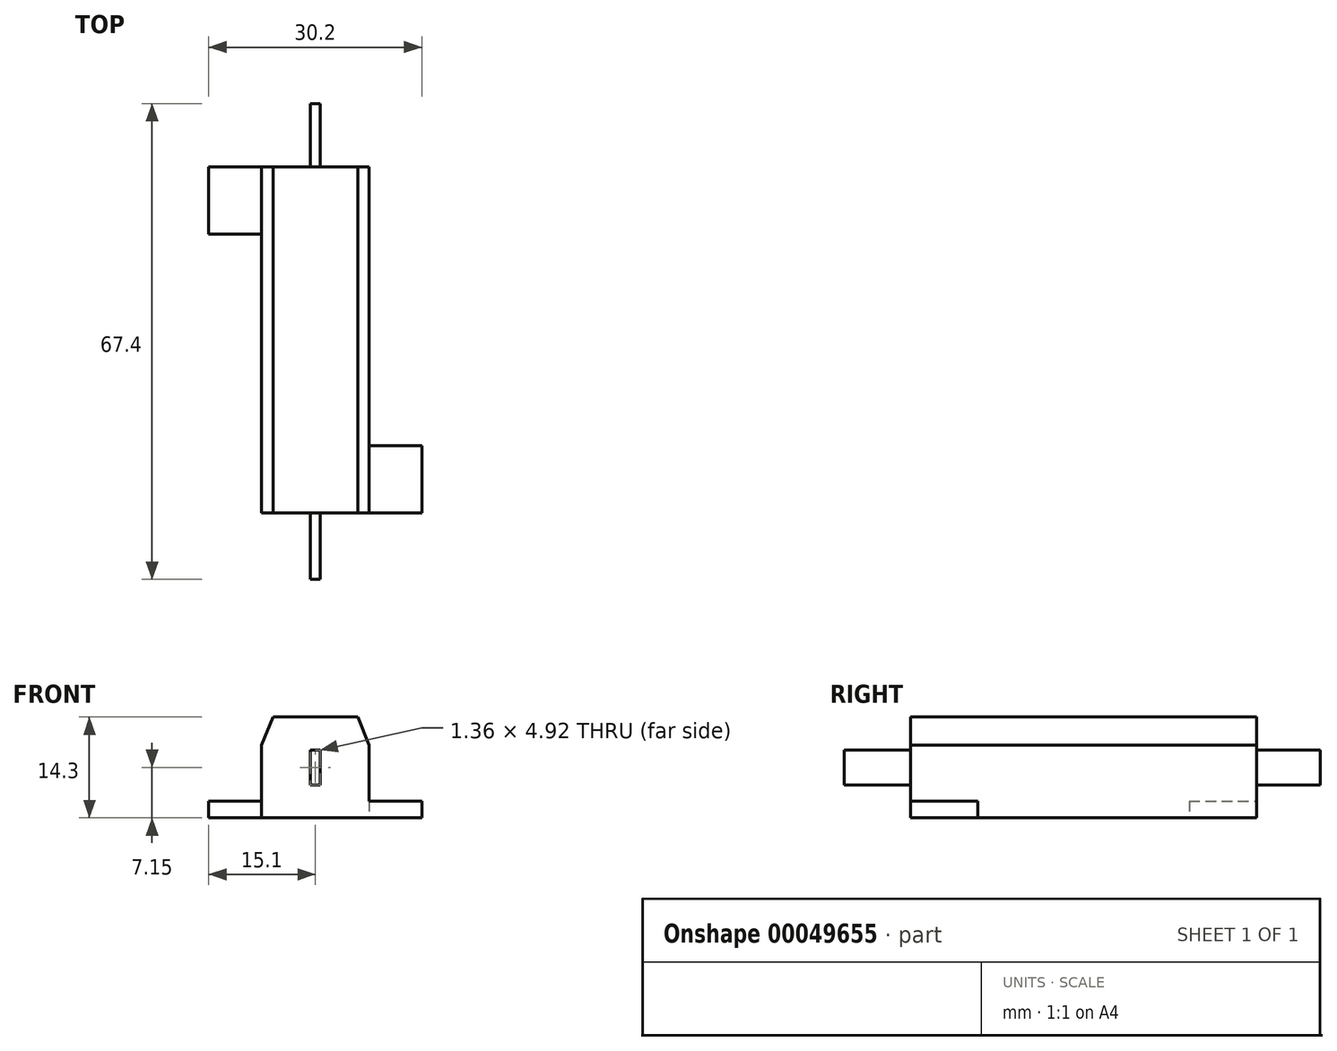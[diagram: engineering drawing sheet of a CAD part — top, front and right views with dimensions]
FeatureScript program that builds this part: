
annotation { "Feature Type Name" : "Feature", "Feature Type Description" : "" }
export const myFeature = defineFeature(function(context is Context, id is Id, definition is map)
    precondition{}
    {
        {
            var Q0;
            Q0=qCreatedBy(makeId("Front.planeOp"),FACE);
            var sketch = newSketch(context, id + "F0", { "sketchPlane" : qUnion([Q0])});
            skLineSegment(sketch, "E0.bottom", {"start": v(0, 0) * mm, "end": v(-15.2, 0) * mm});
            skLineSegment(sketch, "E0.top", {"start": v(0, 2.41) * mm, "end": v(-15.2, 2.4) * mm, "construction": true});
            skLineSegment(sketch, "E0.left", {"start": v(0, 0) * mm, "end": v(0, 2.4) * mm});
            skLineSegment(sketch, "E0.right", {"start": v(-15.2, 0) * mm, "end": v(-15.2, 2.4) * mm});
            skLineSegment(sketch, "E1", {"start": v(-1.6, 14.3) * mm, "end": v(-13.6, 14.3) * mm});
            skLineSegment(sketch, "E2", {"start": v(0, 2.41) * mm, "end": v(0, 10.3) * mm});
            skLineSegment(sketch, "E3", {"start": v(-7.6, 0) * mm, "end": v(-7.6, 14.3) * mm, "construction": true});
            skLineSegment(sketch, "E4", {"start": v(0, 10.3) * mm, "end": v(-1.6, 14.3) * mm});
            skLineSegment(sketch, "E5", {"start": v(-15.2, 2.4) * mm, "end": v(-15.2, 10.3) * mm});
            skLineSegment(sketch, "E6", {"start": v(-15.2, 10.3) * mm, "end": v(-13.6, 14.3) * mm});
            skSolve(sketch);
        }
        {
            var Q0;
            Q0=makeQuery(id+"F0.imprint","IMPRINT",FACE,{"disambiguationData":[TD([[makeQuery(id+"F0.imprint","IMPRINT",EDGE,{"derivedFrom":sQuery(id+"F0.wireOp",EDGE,"E0.bottom")}),-1.0]])]});
            extrude(context, id + "F1", {"entities" : qUnion([Q0]), "depth" : 49 * mm});
        }
        {
            var Q0;
            Q0=makeQuery(id+"F1.opExtrude","SWEPT_FACE",FACE,{"disambiguationData":[OSD([sQuery(id+"F0.wireOp",EDGE,"E0.bottom")])]});
            var sketch = newSketch(context, id + "F2", { "sketchPlane" : qUnion([Q0])});
            skLineSegment(sketch, "E7.bottom", {"start": v(-15.2, 0) * mm, "end": v(-22.7, 0) * mm});
            skLineSegment(sketch, "E7.top", {"start": v(-15.2, 9.53) * mm, "end": v(-22.7, 9.53) * mm});
            skLineSegment(sketch, "E7.left", {"start": v(-15.2, 0) * mm, "end": v(-15.2, 9.53) * mm});
            skLineSegment(sketch, "E7.right", {"start": v(-22.7, 0) * mm, "end": v(-22.7, 9.53) * mm});
            skLineSegment(sketch, "E8.bottom", {"start": v(0, 49) * mm, "end": v(7.5, 49) * mm});
            skLineSegment(sketch, "E8.top", {"start": v(0, 39.47) * mm, "end": v(7.5, 39.47) * mm});
            skLineSegment(sketch, "E8.left", {"start": v(0, 49) * mm, "end": v(0, 39.47) * mm});
            skLineSegment(sketch, "E8.right", {"start": v(7.5, 49) * mm, "end": v(7.5, 39.47) * mm});
            skSolve(sketch);
        }
        {
            var Q0;
            Q0=makeQuery(id+"F2.imprint","IMPRINT",FACE,{"disambiguationData":[TD([[makeQuery(id+"F2.imprint","IMPRINT",EDGE,{"derivedFrom":sQuery(id+"F2.wireOp",EDGE,"E7.bottom")}),-1.0]])]});
            var Q1;
            Q1=makeQuery(id+"F2.imprint","IMPRINT",FACE,{"disambiguationData":[TD([[makeQuery(id+"F2.imprint","IMPRINT",EDGE,{"derivedFrom":sQuery(id+"F2.wireOp",EDGE,"E8.bottom")}),-1.0]])]});
            extrude(context, id + "F3", {"entities" : qUnion([Q0, Q1]), "operationType" : NewBodyOperationType.ADD, "oppositeDirection" : true, "depth" : 2.4 * mm});
        }
        {
            var Q0;
            Q0=makeQuery(id+"F3.boolean.opBoolean","MERGE",FACE,{"derivedFrom":[makeQuery(id+"F1.opExtrude","CAP_FACE",FACE,{"disambiguationData":[OSD([sQuery(id+"F0.wireOp",EDGE,"E0.bottom"),sQuery(id+"F0.wireOp",EDGE,"E0.left"),sQuery(id+"F0.wireOp",EDGE,"E0.right"),sQuery(id+"F0.wireOp",EDGE,"E1"),sQuery(id+"F0.wireOp",EDGE,"E2"),sQuery(id+"F0.wireOp",EDGE,"E4"),sQuery(id+"F0.wireOp",EDGE,"E5"),sQuery(id+"F0.wireOp",EDGE,"E6")])],"isStart":true}),makeQuery(id+"F3.opExtrude","SWEPT_FACE",FACE,{"disambiguationData":[OSD([sQuery(id+"F2.wireOp",EDGE,"E7.bottom")])]})]});
            var sketch = newSketch(context, id + "F4", { "sketchPlane" : qUnion([Q0])});
            skLineSegment(sketch, "E9", {"start": v(7.6, 14.3) * mm, "end": v(7.6, 0) * mm, "construction": true});
            skLineSegment(sketch, "E10.bottom", {"start": v(8.28, 9.61) * mm, "end": v(6.92, 9.61) * mm});
            skLineSegment(sketch, "E10.top", {"start": v(8.28, 4.69) * mm, "end": v(6.92, 4.69) * mm});
            skLineSegment(sketch, "E10.left", {"start": v(8.28, 9.61) * mm, "end": v(8.28, 4.69) * mm});
            skLineSegment(sketch, "E10.right", {"start": v(6.92, 9.61) * mm, "end": v(6.92, 4.69) * mm});
            skPoint(sketch, "E10.middle", {"position": v(7.6, 7.15) * mm});
            skSolve(sketch);
        }
        {
            var Q0;
            Q0=makeQuery(id+"F4.imprint","IMPRINT",FACE,{"disambiguationData":[TD([[makeQuery(id+"F4.imprint","IMPRINT",EDGE,{"derivedFrom":sQuery(id+"F4.wireOp",EDGE,"E10.bottom")}),1.0]])]});
            extrude(context, id + "F5", {"entities" : qUnion([Q0]), "operationType" : NewBodyOperationType.ADD, "depth" : 9 * mm, "hasSecondDirection" : true, "secondDirectionOppositeDirection" : true, "secondDirectionDepth" : 58.4 * mm});
        }
    });
